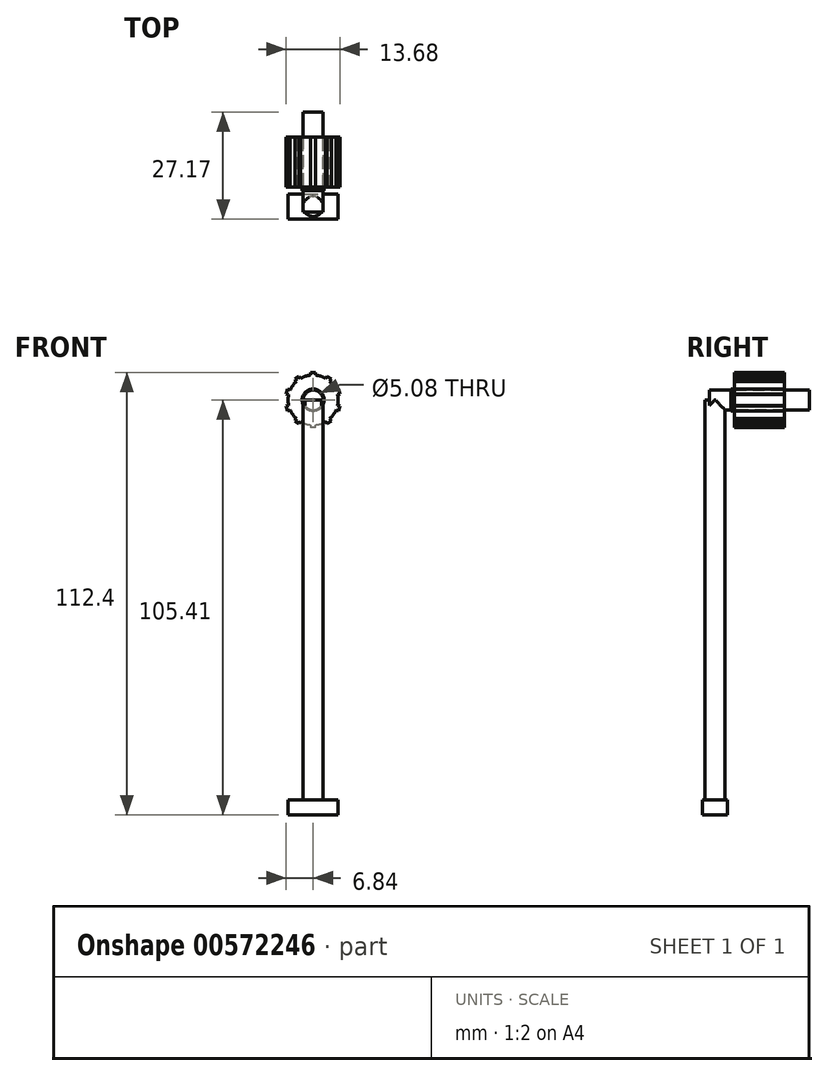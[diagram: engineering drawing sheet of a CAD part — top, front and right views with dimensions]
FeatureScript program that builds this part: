
annotation { "Feature Type Name" : "Feature", "Feature Type Description" : "" }
export const myFeature = defineFeature(function(context is Context, id is Id, definition is map)
    precondition{}
    {
        {
            var Q0;
            Q0=qCreatedBy(makeId("Front.planeOp"),FACE);
            var sketch = newSketch(context, id + "F0", { "sketchPlane" : qUnion([Q0])});
            skArc(sketch, "E0", {"start": v(-0.64, 6.32) * mm, "mid": v(-1.96, 6.04) * mm, "end": v(-3.2, 5.48) * mm});
            skLineSegment(sketch, "E1.bottom", {"start": v(-0.64, 6.99) * mm, "end": v(0.64, 6.99) * mm});
            skLineSegment(sketch, "E1.left", {"start": v(-0.64, 6.99) * mm, "end": v(-0.64, 6.32) * mm});
            skPoint(sketch, "E1.middle", {"position": v(0, 6.35) * mm});
            skPoint(sketch, "E1.top.start.orphan", {"position": v(-0.64, 5.72) * mm});
            skPoint(sketch, "E2.orphan", {"position": v(0.63, 5.72) * mm});
            skLineSegment(sketch, "E3", {"start": v(0.63, 6.32) * mm, "end": v(0.63, 6.99) * mm});
            skLineSegment(sketch, "E4.1.0", {"start": v(-4.62, 5.28) * mm, "end": v(-4.23, 4.74) * mm});
            skLineSegment(sketch, "E4.1.1", {"start": v(-4.62, 5.28) * mm, "end": v(-3.6, 6.02) * mm});
            skLineSegment(sketch, "E4.1.2", {"start": v(-3.2, 5.48) * mm, "end": v(-3.6, 6.02) * mm});
            skLineSegment(sketch, "E4.2.0", {"start": v(-6.84, 1.55) * mm, "end": v(-6.2, 1.35) * mm});
            skLineSegment(sketch, "E4.2.1", {"start": v(-6.84, 1.55) * mm, "end": v(-6.45, 2.76) * mm});
            skLineSegment(sketch, "E4.2.2", {"start": v(-5.81, 2.56) * mm, "end": v(-6.45, 2.76) * mm});
            skLineSegment(sketch, "E4.3.0", {"start": v(-6.45, -2.76) * mm, "end": v(-5.81, -2.56) * mm});
            skLineSegment(sketch, "E4.3.1", {"start": v(-6.45, -2.76) * mm, "end": v(-6.84, -1.55) * mm});
            skLineSegment(sketch, "E4.3.2", {"start": v(-6.2, -1.35) * mm, "end": v(-6.84, -1.55) * mm});
            skLineSegment(sketch, "E4.4.0", {"start": v(-3.6, -6.02) * mm, "end": v(-3.2, -5.48) * mm});
            skLineSegment(sketch, "E4.4.1", {"start": v(-3.6, -6.02) * mm, "end": v(-4.62, -5.28) * mm});
            skLineSegment(sketch, "E4.4.2", {"start": v(-4.23, -4.74) * mm, "end": v(-4.62, -5.28) * mm});
            skLineSegment(sketch, "E4.5.0", {"start": v(0.63, -6.99) * mm, "end": v(0.63, -6.32) * mm});
            skLineSegment(sketch, "E4.5.1", {"start": v(0.63, -6.99) * mm, "end": v(-0.64, -6.99) * mm});
            skLineSegment(sketch, "E4.5.2", {"start": v(-0.63, -6.32) * mm, "end": v(-0.64, -6.99) * mm});
            skLineSegment(sketch, "E4.6.0", {"start": v(4.62, -5.28) * mm, "end": v(4.23, -4.74) * mm});
            skLineSegment(sketch, "E4.6.1", {"start": v(4.62, -5.28) * mm, "end": v(3.6, -6.02) * mm});
            skLineSegment(sketch, "E4.6.2", {"start": v(3.2, -5.48) * mm, "end": v(3.6, -6.02) * mm});
            skLineSegment(sketch, "E4.7.0", {"start": v(6.84, -1.55) * mm, "end": v(6.2, -1.35) * mm});
            skLineSegment(sketch, "E4.7.1", {"start": v(6.84, -1.55) * mm, "end": v(6.45, -2.76) * mm});
            skLineSegment(sketch, "E4.7.2", {"start": v(5.81, -2.56) * mm, "end": v(6.45, -2.76) * mm});
            skLineSegment(sketch, "E4.8.0", {"start": v(6.45, 2.76) * mm, "end": v(5.81, 2.56) * mm});
            skLineSegment(sketch, "E4.8.1", {"start": v(6.45, 2.76) * mm, "end": v(6.84, 1.55) * mm});
            skLineSegment(sketch, "E4.8.2", {"start": v(6.2, 1.35) * mm, "end": v(6.84, 1.55) * mm});
            skLineSegment(sketch, "E4.9.0", {"start": v(3.6, 6.02) * mm, "end": v(3.2, 5.48) * mm});
            skLineSegment(sketch, "E4.9.1", {"start": v(3.6, 6.02) * mm, "end": v(4.62, 5.28) * mm});
            skLineSegment(sketch, "E4.9.2", {"start": v(4.23, 4.74) * mm, "end": v(4.62, 5.28) * mm});
            skArc(sketch, "E5.trimOffspring", {"start": v(-4.23, 4.74) * mm, "mid": v(-5.14, 3.73) * mm, "end": v(-5.81, 2.56) * mm});
            skArc(sketch, "E6.trimOffspring", {"start": v(3.2, 5.48) * mm, "mid": v(1.96, 6.04) * mm, "end": v(0.63, 6.32) * mm});
            skArc(sketch, "E7.trimOffspring", {"start": v(5.81, 2.56) * mm, "mid": v(5.14, 3.73) * mm, "end": v(4.23, 4.74) * mm});
            skArc(sketch, "E8.trimOffspring", {"start": v(-6.2, 1.35) * mm, "mid": v(-6.35, 0) * mm, "end": v(-6.2, -1.35) * mm});
            skArc(sketch, "E9.trimOffspring", {"start": v(0.64, -6.32) * mm, "mid": v(1.96, -6.04) * mm, "end": v(3.2, -5.48) * mm});
            skArc(sketch, "E10.trimOffspring", {"start": v(-3.2, -5.48) * mm, "mid": v(-1.96, -6.04) * mm, "end": v(-0.64, -6.32) * mm});
            skArc(sketch, "E11.trimOffspring", {"start": v(-5.81, -2.56) * mm, "mid": v(-5.14, -3.73) * mm, "end": v(-4.23, -4.74) * mm});
            skArc(sketch, "E12.trimOffspring", {"start": v(4.23, -4.74) * mm, "mid": v(5.14, -3.73) * mm, "end": v(5.81, -2.56) * mm});
            skArc(sketch, "E13.trimOffspring", {"start": v(6.2, -1.35) * mm, "mid": v(6.35, 0) * mm, "end": v(6.2, 1.35) * mm});
            skSolve(sketch);
        }
        {
            var Q0;
            Q0 = qSketchRegion(id + "F0", true);
            extrude(context, id + "F1", {"entities" : qUnion([Q0]), "endBound" : BoundingType.SYMMETRIC, "depth" : 12.7 * mm, "offsetDistance" : 25.4 * mm});
        }
        {
            var Q0;
            Q0=makeQuery(id+"F1.opExtrude","CAP_FACE",FACE,{"disambiguationData":[OSD([sQuery(id+"F0.wireOp",EDGE,"E0"),sQuery(id+"F0.wireOp",EDGE,"E1.bottom"),sQuery(id+"F0.wireOp",EDGE,"E1.left"),sQuery(id+"F0.wireOp",EDGE,"E3"),sQuery(id+"F0.wireOp",EDGE,"E4.1.0"),sQuery(id+"F0.wireOp",EDGE,"E4.1.1"),sQuery(id+"F0.wireOp",EDGE,"E4.1.2"),sQuery(id+"F0.wireOp",EDGE,"E4.2.0"),sQuery(id+"F0.wireOp",EDGE,"E4.2.1"),sQuery(id+"F0.wireOp",EDGE,"E4.2.2"),sQuery(id+"F0.wireOp",EDGE,"E4.3.0"),sQuery(id+"F0.wireOp",EDGE,"E4.3.1"),sQuery(id+"F0.wireOp",EDGE,"E4.3.2"),sQuery(id+"F0.wireOp",EDGE,"E4.4.0"),sQuery(id+"F0.wireOp",EDGE,"E4.4.1"),sQuery(id+"F0.wireOp",EDGE,"E4.4.2"),sQuery(id+"F0.wireOp",EDGE,"E4.5.0"),sQuery(id+"F0.wireOp",EDGE,"E4.5.1"),sQuery(id+"F0.wireOp",EDGE,"E4.5.2"),sQuery(id+"F0.wireOp",EDGE,"E4.6.0"),sQuery(id+"F0.wireOp",EDGE,"E4.6.1"),sQuery(id+"F0.wireOp",EDGE,"E4.6.2"),sQuery(id+"F0.wireOp",EDGE,"E4.7.0"),sQuery(id+"F0.wireOp",EDGE,"E4.7.1"),sQuery(id+"F0.wireOp",EDGE,"E4.7.2"),sQuery(id+"F0.wireOp",EDGE,"E4.8.0"),sQuery(id+"F0.wireOp",EDGE,"E4.8.1"),sQuery(id+"F0.wireOp",EDGE,"E4.8.2"),sQuery(id+"F0.wireOp",EDGE,"E4.9.0"),sQuery(id+"F0.wireOp",EDGE,"E4.9.1"),sQuery(id+"F0.wireOp",EDGE,"E4.9.2"),sQuery(id+"F0.wireOp",EDGE,"E5.trimOffspring"),sQuery(id+"F0.wireOp",EDGE,"E6.trimOffspring"),sQuery(id+"F0.wireOp",EDGE,"E7.trimOffspring"),sQuery(id+"F0.wireOp",EDGE,"E8.trimOffspring"),sQuery(id+"F0.wireOp",EDGE,"E9.trimOffspring"),sQuery(id+"F0.wireOp",EDGE,"E10.trimOffspring"),sQuery(id+"F0.wireOp",EDGE,"E11.trimOffspring"),sQuery(id+"F0.wireOp",EDGE,"E12.trimOffspring"),sQuery(id+"F0.wireOp",EDGE,"E13.trimOffspring")])],"isStart":false});
            var sketch = newSketch(context, id + "F2", { "sketchPlane" : qUnion([Q0])});
            skCircle(sketch, "E14", {"center": v(0, 0) * mm, "radius": 2.54 * mm});
            skSolve(sketch);
        }
        {
            var Q0;
            Q0 = qSketchRegion(id + "F2", true);
            extrude(context, id + "F3", {"entities" : qUnion([Q0]), "operationType" : NewBodyOperationType.REMOVE, "oppositeDirection" : true, "depth" : 25.4 * mm, "offsetDistance" : 25.4 * mm});
        }
        {
            var Q0;
            Q0=qCreatedBy(makeId("Front.planeOp"),FACE);
            var sketch = newSketch(context, id + "F4", { "sketchPlane" : qUnion([Q0])});
            skCircle(sketch, "E15", {"center": v(0, 0) * mm, "radius": 2.53 * mm});
            skSolve(sketch);
        }
        {
            var Q0;
            Q0 = qSketchRegion(id + "F4", true);
            extrude(context, id + "F5", {"entities" : qUnion([Q0]), "endBound" : BoundingType.SYMMETRIC, "depth" : 25.4 * mm, "offsetDistance" : 25.4 * mm});
        }
        {
            var Q0;
            Q0=qCreatedBy(makeId("Front.planeOp"),FACE);
            cPlane(context, id + "F6", {"entities" : qUnion([Q0]), "cplaneType" : CPlaneType.OFFSET, "offset" : 6.86 * mm, "width" : 152.4 * mm, "height" : 152.4 * mm});
        }
        {
            var Q0;
            Q0=qCreatedBy(id+"F6.planeOp",FACE);
            var sketch = newSketch(context, id + "F7", { "sketchPlane" : qUnion([Q0])});
            skCircle(sketch, "E16", {"center": v(0, 0) * mm, "radius": 2.8 * mm});
            skSolve(sketch);
        }
        {
            var Q0;
            Q0 = qSketchRegion(id + "F7", true);
            extrude(context, id + "F8", {"entities" : qUnion([Q0]), "operationType" : NewBodyOperationType.ADD, "endBound" : BoundingType.SYMMETRIC, "depth" : 0.76 * mm, "offsetDistance" : 25.4 * mm});
        }
        {
            var Q0;
            Q0=qCreatedBy(makeId("Top.planeOp"),FACE);
            cPlane(context, id + "F9", {"entities" : qUnion([Q0]), "cplaneType" : CPlaneType.OFFSET, "offset" : 101.6 * mm, "oppositeDirection" : true, "width" : 152.4 * mm, "height" : 152.4 * mm});
        }
        {
            var Q0;
            Q0=qCreatedBy(id+"F9.planeOp",FACE);
            var sketch = newSketch(context, id + "F10", { "sketchPlane" : qUnion([Q0])});
            skCircle(sketch, "E17", {"center": v(0, -11.3) * mm, "radius": 2.54 * mm});
            skSolve(sketch);
        }
        {
            var Q0;
            Q0 = qSketchRegion(id + "F10", true);
            extrude(context, id + "F11", {"entities" : qUnion([Q0]), "operationType" : NewBodyOperationType.ADD, "depth" : 101.6 * mm, "offsetDistance" : 25.4 * mm});
        }
        {
            var Q0;
            Q0=makeQuery(id+"F11.opExtrude","CAP_FACE",FACE,{"disambiguationData":[OSD([sQuery(id+"F10.wireOp",EDGE,"E17")])],"isStart":true});
            var sketch = newSketch(context, id + "F12", { "sketchPlane" : qUnion([Q0])});
            skLineSegment(sketch, "E18", {"start": v(0, 13.84) * mm, "end": v(0, 8.76) * mm});
            skLineSegment(sketch, "E19.bottom", {"start": v(-6.35, 14.47) * mm, "end": v(6.35, 14.47) * mm});
            skLineSegment(sketch, "E19.top", {"start": v(-6.35, 8.12) * mm, "end": v(6.35, 8.12) * mm});
            skLineSegment(sketch, "E19.left", {"start": v(-6.35, 14.47) * mm, "end": v(-6.35, 8.12) * mm});
            skLineSegment(sketch, "E19.right", {"start": v(6.35, 14.47) * mm, "end": v(6.35, 8.12) * mm});
            skPoint(sketch, "E19.middle", {"position": v(0, 11.3) * mm});
            skSolve(sketch);
        }
        {
            var Q0;
            Q0 = qSketchRegion(id + "F12", true);
            extrude(context, id + "F13", {"entities" : qUnion([Q0]), "operationType" : NewBodyOperationType.ADD, "depth" : 3.8 * mm, "offsetDistance" : 25.4 * mm});
        }
    });
